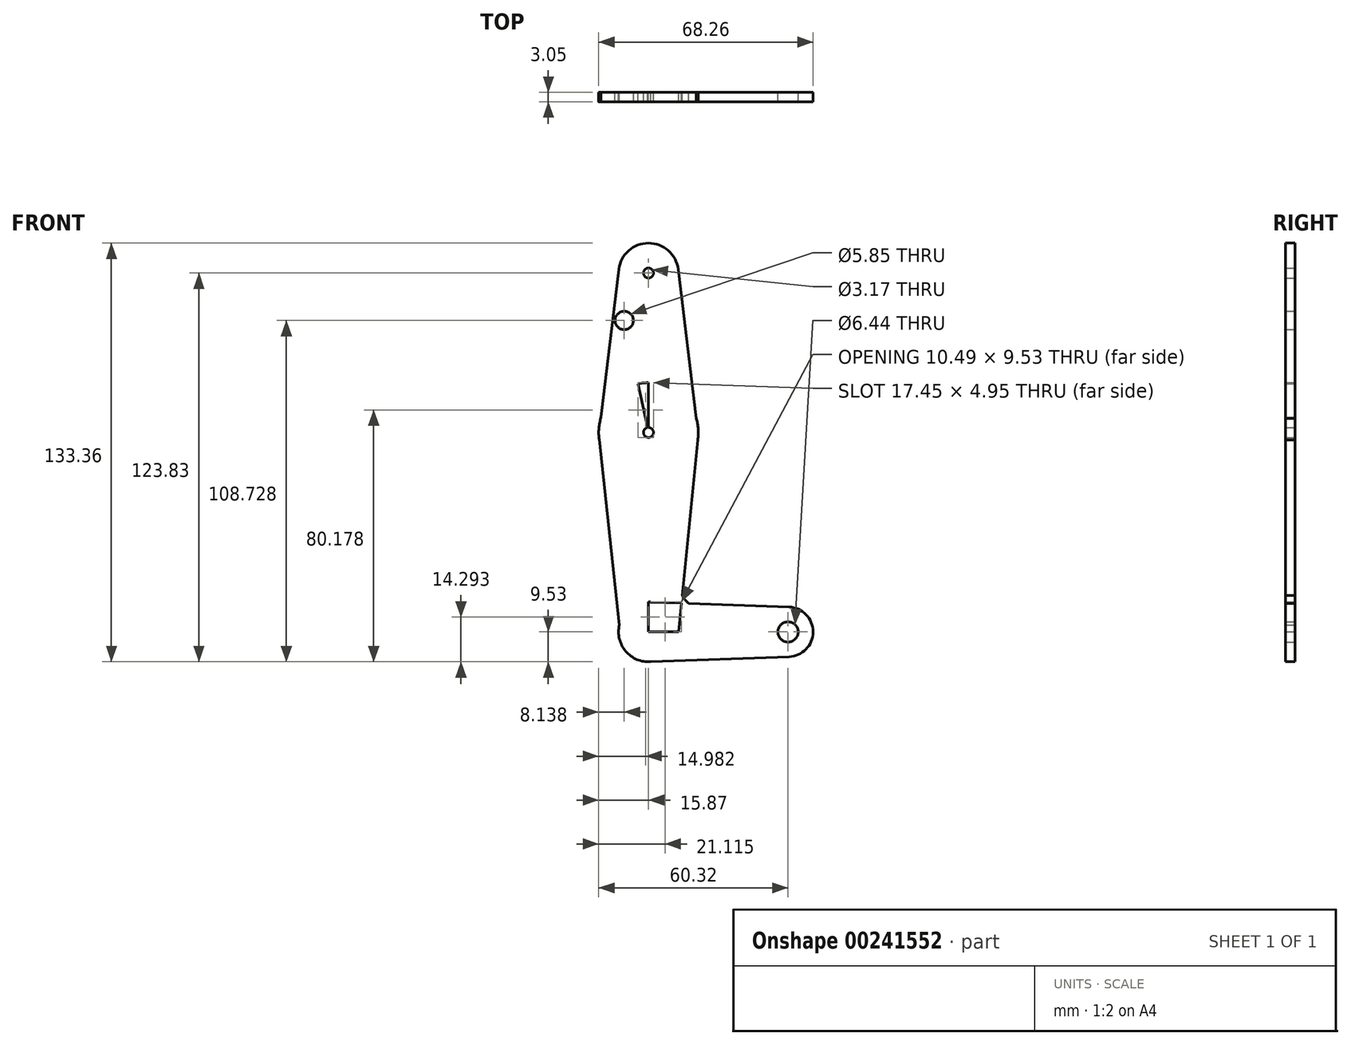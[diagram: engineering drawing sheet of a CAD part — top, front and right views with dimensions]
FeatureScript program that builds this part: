
annotation { "Feature Type Name" : "Feature", "Feature Type Description" : "" }
export const myFeature = defineFeature(function(context is Context, id is Id, definition is map)
    precondition{}
    {
        {
            var Q0;
            Q0=qCreatedBy(makeId("Front.planeOp"),FACE);
            var sketch = newSketch(context, id + "F0", { "sketchPlane" : qUnion([Q0])});
            skLineSegment(sketch, "E0", {"start": v(0, 114.3) * mm, "end": v(0, 0) * mm});
            skLineSegment(sketch, "E1", {"start": v(0, 0) * mm, "end": v(44.45, 0) * mm});
            skCircle(sketch, "E2", {"center": v(0, 0) * mm, "radius": 9.53 * mm});
            skCircle(sketch, "E3", {"center": v(44.45, 0) * mm, "radius": 7.94 * mm});
            skCircle(sketch, "E4", {"center": v(0, 63.5) * mm, "radius": 15.88 * mm});
            skLineSegment(sketch, "E5", {"start": v(0, 63.5) * mm, "end": v(0, 0) * mm});
            skCircle(sketch, "E6", {"center": v(0, 114.3) * mm, "radius": 9.53 * mm});
            skLineSegment(sketch, "E7", {"start": v(-15.83, 62.33) * mm, "end": v(-9.46, 115.44) * mm});
            skLineSegment(sketch, "E8", {"start": v(15.86, 62.72) * mm, "end": v(9.46, 115.45) * mm});
            skLineSegment(sketch, "E9", {"start": v(-15.83, 62.33) * mm, "end": v(-8.57, -4.16) * mm});
            skLineSegment(sketch, "E10", {"start": v(15.86, 62.72) * mm, "end": v(9.57, 0) * mm});
            skLineSegment(sketch, "E11", {"start": v(0, 9.53) * mm, "end": v(44.73, 7.93) * mm});
            skLineSegment(sketch, "E12", {"start": v(0, -9.52) * mm, "end": v(44.73, -7.93) * mm});
            skCircle(sketch, "E13", {"center": v(-7.73, 99.2) * mm, "radius": 2.92 * mm});
            skCircle(sketch, "E14", {"center": v(0, 114.3) * mm, "radius": 1.59 * mm});
            skCircle(sketch, "E15", {"center": v(0, 63.5) * mm, "radius": 1.59 * mm});
            skCircle(sketch, "E16", {"center": v(44.45, 0) * mm, "radius": 3.22 * mm});
            skLineSegment(sketch, "E17", {"start": v(0, 63.5) * mm, "end": v(-7.73, 99.2) * mm});
            skArc(sketch, "E18", {"start": v(11.6, 20.2) * mm, "mid": v(12.03, 9.81) * mm, "end": v(22.37, 8.73) * mm});
            skSolve(sketch);
        }
        {
            var Q0;
            Q0 = qSketchRegion(id + "F0", true);
            extrude(context, id + "F1", {"entities" : qUnion([Q0]), "depth" : 3.05 * mm});
        }
    });
